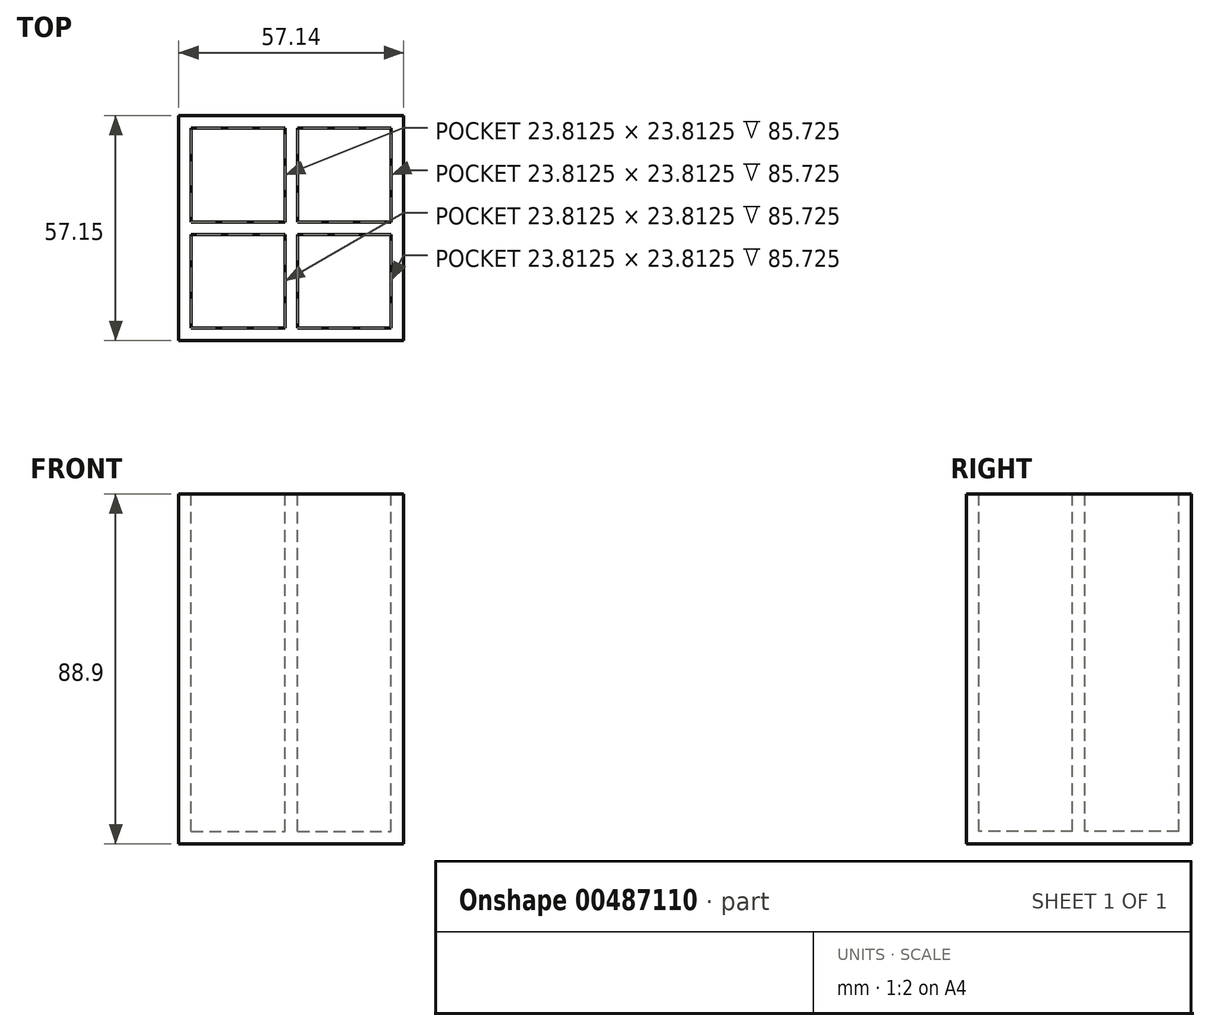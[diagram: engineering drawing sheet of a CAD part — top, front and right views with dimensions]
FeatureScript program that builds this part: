
annotation { "Feature Type Name" : "Feature", "Feature Type Description" : "" }
export const myFeature = defineFeature(function(context is Context, id is Id, definition is map)
    precondition{}
    {
        {
            var Q0;
            Q0=qCreatedBy(makeId("Front.planeOp"),FACE);
            var sketch = newSketch(context, id + "F0", { "sketchPlane" : qUnion([Q0])});
            skLineSegment(sketch, "E0.bottom", {"start": v(-28.57, -44.45) * mm, "end": v(28.58, -44.45) * mm});
            skLineSegment(sketch, "E0.top", {"start": v(-28.58, 44.45) * mm, "end": v(28.57, 44.45) * mm});
            skLineSegment(sketch, "E0.left", {"start": v(-28.58, -44.45) * mm, "end": v(-28.58, 44.45) * mm});
            skLineSegment(sketch, "E0.right", {"start": v(28.58, -44.45) * mm, "end": v(28.57, 44.45) * mm});
            skPoint(sketch, "E0.middle", {"position": v(0, 0) * mm});
            skSolve(sketch);
        }
        {
            var Q0;
            Q0=makeQuery(id+"F0.imprint","IMPRINT",FACE,{"disambiguationData":[TD([[makeQuery(id+"F0.imprint","IMPRINT",EDGE,{"derivedFrom":sQuery(id+"F0.wireOp",EDGE,"E0.bottom")}),1.0]])]});
            extrude(context, id + "F1", {"entities" : qUnion([Q0]), "depth" : 57.15 * mm});
        }
        {
            var Q0;
            Q0=makeQuery(id+"F1.opExtrude","SWEPT_FACE",FACE,{"disambiguationData":[OSD([sQuery(id+"F0.wireOp",EDGE,"E0.top")])]});
            var sketch = newSketch(context, id + "F2", { "sketchPlane" : qUnion([Q0])});
            skLineSegment(sketch, "E1.bottom", {"start": v(-25.4, -3.18) * mm, "end": v(-1.59, -3.18) * mm});
            skLineSegment(sketch, "E1.top", {"start": v(-25.4, -26.99) * mm, "end": v(-1.59, -26.99) * mm});
            skLineSegment(sketch, "E1.left", {"start": v(-25.4, -3.18) * mm, "end": v(-25.4, -26.99) * mm});
            skLineSegment(sketch, "E1.right", {"start": v(-1.59, -3.17) * mm, "end": v(-1.59, -26.99) * mm});
            skSolve(sketch);
        }
        {
            var Q0;
            Q0 = qSketchRegion(id + "F2", true);
            extrude(context, id + "F3", {"entities" : qUnion([Q0]), "operationType" : NewBodyOperationType.REMOVE, "oppositeDirection" : true, "depth" : 85.72 * mm});
        }
        {
            var Q0;
            Q0=makeQuery(id+"F1.opExtrude","SWEPT_FACE",FACE,{"disambiguationData":[OSD([sQuery(id+"F0.wireOp",EDGE,"E0.top")])]});
            var sketch = newSketch(context, id + "F4", { "sketchPlane" : qUnion([Q0])});
            skLineSegment(sketch, "E2.bottom", {"start": v(1.59, -3.18) * mm, "end": v(25.4, -3.18) * mm});
            skLineSegment(sketch, "E2.top", {"start": v(1.59, -26.99) * mm, "end": v(25.4, -26.99) * mm});
            skLineSegment(sketch, "E2.left", {"start": v(1.59, -3.18) * mm, "end": v(1.59, -26.99) * mm});
            skLineSegment(sketch, "E2.right", {"start": v(25.4, -3.17) * mm, "end": v(25.4, -26.99) * mm});
            skSolve(sketch);
        }
        {
            var Q0;
            Q0 = qSketchRegion(id + "F4", true);
            extrude(context, id + "F5", {"entities" : qUnion([Q0]), "operationType" : NewBodyOperationType.REMOVE, "oppositeDirection" : true, "depth" : 85.72 * mm});
        }
        {
            var Q0;
            Q0=makeQuery(id+"F1.opExtrude","SWEPT_FACE",FACE,{"disambiguationData":[OSD([sQuery(id+"F0.wireOp",EDGE,"E0.top")])]});
            var sketch = newSketch(context, id + "F6", { "sketchPlane" : qUnion([Q0])});
            skLineSegment(sketch, "E3.bottom", {"start": v(-25.4, -30.16) * mm, "end": v(-1.59, -30.16) * mm});
            skLineSegment(sketch, "E3.top", {"start": v(-25.4, -53.98) * mm, "end": v(-1.59, -53.98) * mm});
            skLineSegment(sketch, "E3.left", {"start": v(-25.4, -30.16) * mm, "end": v(-25.4, -53.98) * mm});
            skLineSegment(sketch, "E3.right", {"start": v(-1.59, -30.16) * mm, "end": v(-1.59, -53.98) * mm});
            skSolve(sketch);
        }
        {
            var Q0;
            Q0 = qSketchRegion(id + "F6", true);
            extrude(context, id + "F7", {"entities" : qUnion([Q0]), "operationType" : NewBodyOperationType.REMOVE, "oppositeDirection" : true, "depth" : 85.72 * mm});
        }
        {
            var Q0;
            Q0=makeQuery(id+"F1.opExtrude","SWEPT_FACE",FACE,{"disambiguationData":[OSD([sQuery(id+"F0.wireOp",EDGE,"E0.top")])]});
            var sketch = newSketch(context, id + "F8", { "sketchPlane" : qUnion([Q0])});
            skLineSegment(sketch, "E4.bottom", {"start": v(1.59, -30.16) * mm, "end": v(25.4, -30.16) * mm});
            skLineSegment(sketch, "E4.top", {"start": v(1.59, -53.98) * mm, "end": v(25.4, -53.98) * mm});
            skLineSegment(sketch, "E4.left", {"start": v(1.59, -30.16) * mm, "end": v(1.59, -53.98) * mm});
            skLineSegment(sketch, "E4.right", {"start": v(25.4, -30.16) * mm, "end": v(25.4, -53.98) * mm});
            skSolve(sketch);
        }
        {
            var Q0;
            Q0 = qSketchRegion(id + "F8", true);
            extrude(context, id + "F9", {"entities" : qUnion([Q0]), "operationType" : NewBodyOperationType.REMOVE, "oppositeDirection" : true, "depth" : 85.72 * mm});
        }
    });
